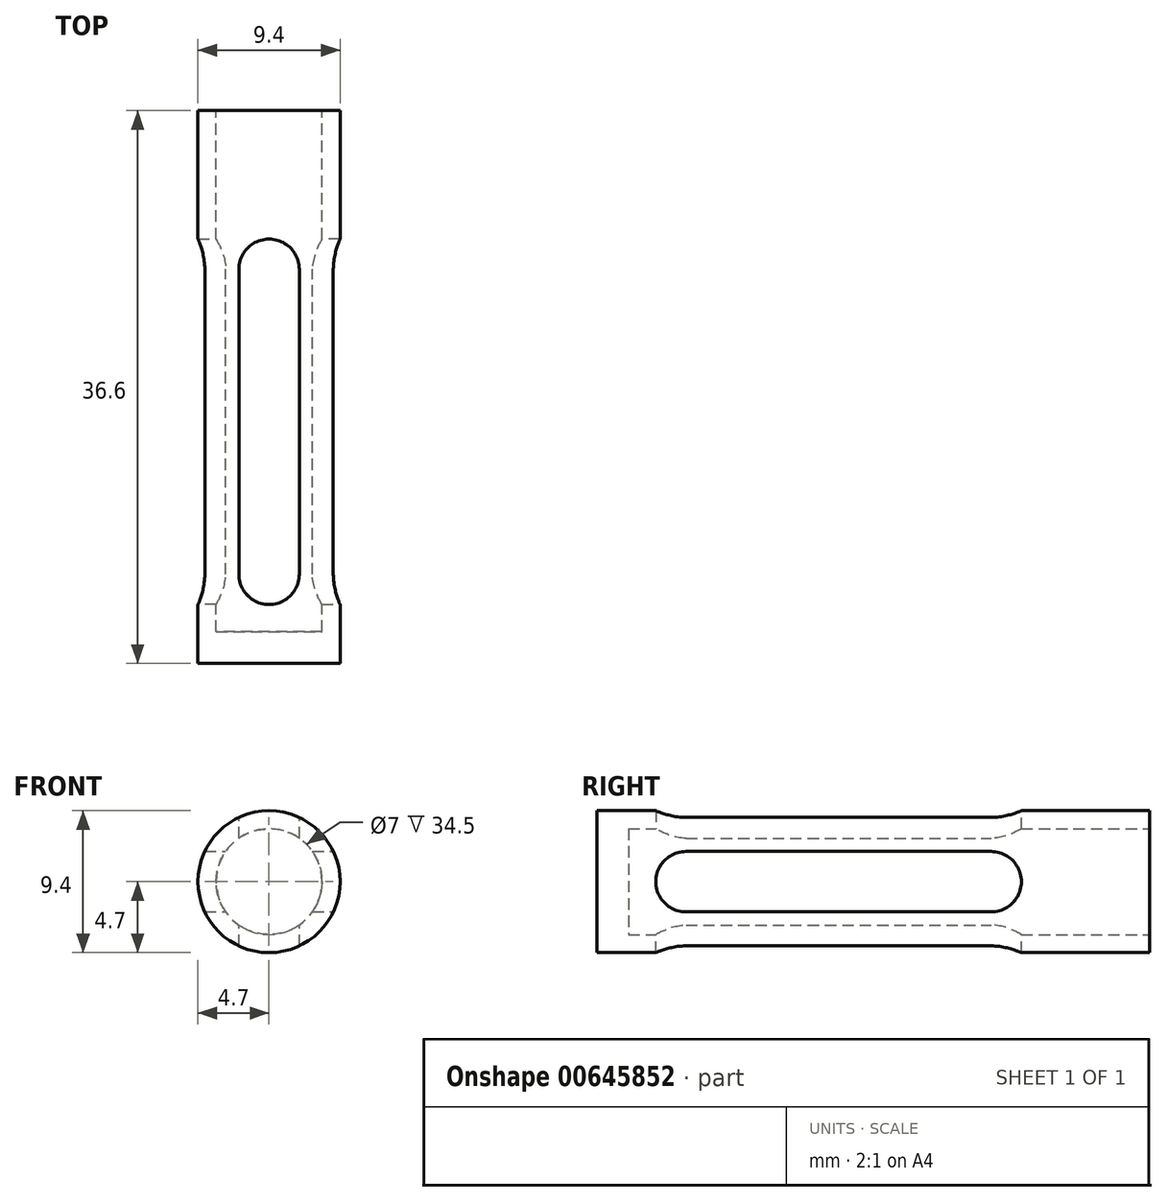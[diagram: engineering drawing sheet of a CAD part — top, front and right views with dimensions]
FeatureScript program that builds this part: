
annotation { "Feature Type Name" : "Feature", "Feature Type Description" : "" }
export const myFeature = defineFeature(function(context is Context, id is Id, definition is map)
    precondition{}
    {
        {
            var Q0;
            Q0=qCreatedBy(makeId("Front.planeOp"),FACE);
            var sketch = newSketch(context, id + "F0", { "sketchPlane" : qUnion([Q0])});
            skCircle(sketch, "E0", {"center": v(0, 0) * mm, "radius": 4.7 * mm});
            skSolve(sketch);
        }
        {
            var Q0;
            Q0 = qSketchRegion(id + "F0", true);
            extrude(context, id + "F1", {"entities" : qUnion([Q0]), "depth" : 36.6 * mm, "offsetDistance" : 25 * mm});
        }
        {
            var Q0;
            Q0=makeQuery(id+"F1.opExtrude","CAP_FACE",FACE,{"disambiguationData":[OSD([sQuery(id+"F0.wireOp",EDGE,"E0")])],"isStart":true});
            var sketch = newSketch(context, id + "F2", { "sketchPlane" : qUnion([Q0])});
            skCircle(sketch, "E1", {"center": v(0, 0) * mm, "radius": 3.5 * mm});
            skCircle(sketch, "E2.0", {"center": v(0, 0) * mm, "radius": 4.7 * mm, "construction": true});
            skSolve(sketch);
        }
        {
            var Q0;
            Q0=makeQuery(id+"F2.imprint","IMPRINT",FACE,{"disambiguationData":[TD([[makeQuery(id+"F2.imprint","IMPRINT",EDGE,{"derivedFrom":sQuery(id+"F2.wireOp",EDGE,"E1")}),1.0]])]});
            extrude(context, id + "F3", {"entities" : qUnion([Q0]), "operationType" : NewBodyOperationType.REMOVE, "oppositeDirection" : true, "depth" : 34.5 * mm, "offsetDistance" : 25 * mm});
        }
        {
            var Q0;
            Q0=qCreatedBy(makeId("Top.planeOp"),FACE);
            var sketch = newSketch(context, id + "F4", { "sketchPlane" : qUnion([Q0])});
            skLineSegment(sketch, "E3.bottom", {"start": v(-2, -32.7) * mm, "end": v(2, -32.7) * mm});
            skLineSegment(sketch, "E3.top", {"start": v(-2, -8.5) * mm, "end": v(2, -8.5) * mm});
            skLineSegment(sketch, "E3.left", {"start": v(-2, -32.7) * mm, "end": v(-2, -8.5) * mm});
            skLineSegment(sketch, "E3.right", {"start": v(2, -32.7) * mm, "end": v(2, -8.5) * mm});
            skLineSegment(sketch, "E4.0", {"start": v(4.7, -36.6) * mm, "end": v(-4.7, -36.6) * mm, "construction": true});
            skLineSegment(sketch, "E5.0", {"start": v(4.7, 0) * mm, "end": v(-4.7, 0) * mm, "construction": true});
            skSolve(sketch);
        }
        {
            var Q0;
            Q0 = qSketchRegion(id + "F4", true);
            extrude(context, id + "F5", {"entities" : qUnion([Q0]), "operationType" : NewBodyOperationType.REMOVE, "endBound" : BoundingType.SYMMETRIC, "oppositeDirection" : true, "depth" : 25 * mm, "offsetDistance" : 25 * mm});
        }
        {
            var Q0;
            Q0=qCreatedBy(makeId("Right.planeOp"),FACE);
            var sketch = newSketch(context, id + "F6", { "sketchPlane" : qUnion([Q0])});
            skLineSegment(sketch, "E6.bottom", {"start": v(-8.5, 2) * mm, "end": v(-32.7, 2) * mm});
            skLineSegment(sketch, "E6.top", {"start": v(-8.5, -2) * mm, "end": v(-32.7, -2) * mm});
            skLineSegment(sketch, "E6.left", {"start": v(-8.5, 2) * mm, "end": v(-8.5, -2) * mm});
            skLineSegment(sketch, "E6.right", {"start": v(-32.7, 2) * mm, "end": v(-32.7, -2) * mm});
            skLineSegment(sketch, "E7.0", {"start": v(-36.6, -4.7) * mm, "end": v(-36.6, 4.7) * mm, "construction": true});
            skLineSegment(sketch, "E8.0", {"start": v(0, -4.7) * mm, "end": v(0, 4.7) * mm, "construction": true});
            skSolve(sketch);
        }
        {
            var Q0;
            Q0 = qSketchRegion(id + "F6", true);
            extrude(context, id + "F7", {"entities" : qUnion([Q0]), "operationType" : NewBodyOperationType.REMOVE, "endBound" : BoundingType.SYMMETRIC, "oppositeDirection" : true, "depth" : 25 * mm, "offsetDistance" : 25 * mm});
        }
        {
            var Q0;
            Q0=makeQuery(id+"F5.boolean.opBoolean","COPY",EDGE,{"disambiguationData":[OD(0.0)],"derivedFrom":makeQuery(id+"F5.opExtrude","SWEPT_EDGE",EDGE,{"disambiguationData":[OSD([sQuery(id+"F4.wireOp",EDGE,"E3.top"),sQuery(id+"F4.wireOp",EDGE,"E3.right")])]})});
            var Q1;
            Q1=makeQuery(id+"F5.boolean.opBoolean","COPY",EDGE,{"disambiguationData":[OD(0.0)],"derivedFrom":makeQuery(id+"F5.opExtrude","SWEPT_EDGE",EDGE,{"disambiguationData":[OSD([sQuery(id+"F4.wireOp",EDGE,"E3.top"),sQuery(id+"F4.wireOp",EDGE,"E3.left")])]})});
            var Q2;
            Q2=makeQuery(id+"F7.boolean.opBoolean","COPY",EDGE,{"disambiguationData":[OD(1.0)],"derivedFrom":makeQuery(id+"F7.opExtrude","SWEPT_EDGE",EDGE,{"disambiguationData":[OSD([sQuery(id+"F6.wireOp",EDGE,"E6.top"),sQuery(id+"F6.wireOp",EDGE,"E6.left")])]})});
            var Q3;
            Q3=makeQuery(id+"F7.boolean.opBoolean","COPY",EDGE,{"disambiguationData":[OD(1.0)],"derivedFrom":makeQuery(id+"F7.opExtrude","SWEPT_EDGE",EDGE,{"disambiguationData":[OSD([sQuery(id+"F6.wireOp",EDGE,"E6.bottom"),sQuery(id+"F6.wireOp",EDGE,"E6.left")])]})});
            var Q4;
            Q4=makeQuery(id+"F7.boolean.opBoolean","COPY",EDGE,{"disambiguationData":[OD(0.0)],"derivedFrom":makeQuery(id+"F7.opExtrude","SWEPT_EDGE",EDGE,{"disambiguationData":[OSD([sQuery(id+"F6.wireOp",EDGE,"E6.bottom"),sQuery(id+"F6.wireOp",EDGE,"E6.left")])]})});
            var Q5;
            Q5=makeQuery(id+"F7.boolean.opBoolean","COPY",EDGE,{"disambiguationData":[OD(0.0)],"derivedFrom":makeQuery(id+"F7.opExtrude","SWEPT_EDGE",EDGE,{"disambiguationData":[OSD([sQuery(id+"F6.wireOp",EDGE,"E6.top"),sQuery(id+"F6.wireOp",EDGE,"E6.left")])]})});
            var Q6;
            Q6=makeQuery(id+"F5.boolean.opBoolean","COPY",EDGE,{"disambiguationData":[OD(1.0)],"derivedFrom":makeQuery(id+"F5.opExtrude","SWEPT_EDGE",EDGE,{"disambiguationData":[OSD([sQuery(id+"F4.wireOp",EDGE,"E3.top"),sQuery(id+"F4.wireOp",EDGE,"E3.right")])]})});
            var Q7;
            Q7=makeQuery(id+"F5.boolean.opBoolean","COPY",EDGE,{"disambiguationData":[OD(1.0)],"derivedFrom":makeQuery(id+"F5.opExtrude","SWEPT_EDGE",EDGE,{"disambiguationData":[OSD([sQuery(id+"F4.wireOp",EDGE,"E3.top"),sQuery(id+"F4.wireOp",EDGE,"E3.left")])]})});
            var Q8;
            Q8=makeQuery(id+"F7.boolean.opBoolean","COPY",EDGE,{"disambiguationData":[OD(0.0)],"derivedFrom":makeQuery(id+"F7.opExtrude","SWEPT_EDGE",EDGE,{"disambiguationData":[OSD([sQuery(id+"F6.wireOp",EDGE,"E6.bottom"),sQuery(id+"F6.wireOp",EDGE,"E6.right")])]})});
            var Q9;
            Q9=makeQuery(id+"F7.boolean.opBoolean","COPY",EDGE,{"disambiguationData":[OD(0.0)],"derivedFrom":makeQuery(id+"F7.opExtrude","SWEPT_EDGE",EDGE,{"disambiguationData":[OSD([sQuery(id+"F6.wireOp",EDGE,"E6.top"),sQuery(id+"F6.wireOp",EDGE,"E6.right")])]})});
            var Q10;
            Q10=makeQuery(id+"F5.boolean.opBoolean","COPY",EDGE,{"disambiguationData":[OD(0.0)],"derivedFrom":makeQuery(id+"F5.opExtrude","SWEPT_EDGE",EDGE,{"disambiguationData":[OSD([sQuery(id+"F4.wireOp",EDGE,"E3.bottom"),sQuery(id+"F4.wireOp",EDGE,"E3.left")])]})});
            var Q11;
            Q11=makeQuery(id+"F5.boolean.opBoolean","COPY",EDGE,{"disambiguationData":[OD(0.0)],"derivedFrom":makeQuery(id+"F5.opExtrude","SWEPT_EDGE",EDGE,{"disambiguationData":[OSD([sQuery(id+"F4.wireOp",EDGE,"E3.bottom"),sQuery(id+"F4.wireOp",EDGE,"E3.right")])]})});
            var Q12;
            Q12=makeQuery(id+"F7.boolean.opBoolean","COPY",EDGE,{"disambiguationData":[OD(1.0)],"derivedFrom":makeQuery(id+"F7.opExtrude","SWEPT_EDGE",EDGE,{"disambiguationData":[OSD([sQuery(id+"F6.wireOp",EDGE,"E6.top"),sQuery(id+"F6.wireOp",EDGE,"E6.right")])]})});
            var Q13;
            Q13=makeQuery(id+"F5.boolean.opBoolean","COPY",EDGE,{"disambiguationData":[OD(1.0)],"derivedFrom":makeQuery(id+"F5.opExtrude","SWEPT_EDGE",EDGE,{"disambiguationData":[OSD([sQuery(id+"F4.wireOp",EDGE,"E3.bottom"),sQuery(id+"F4.wireOp",EDGE,"E3.right")])]})});
            var Q14;
            Q14=makeQuery(id+"F5.boolean.opBoolean","COPY",EDGE,{"disambiguationData":[OD(1.0)],"derivedFrom":makeQuery(id+"F5.opExtrude","SWEPT_EDGE",EDGE,{"disambiguationData":[OSD([sQuery(id+"F4.wireOp",EDGE,"E3.bottom"),sQuery(id+"F4.wireOp",EDGE,"E3.left")])]})});
            var Q15;
            Q15=makeQuery(id+"F7.boolean.opBoolean","COPY",EDGE,{"disambiguationData":[OD(1.0)],"derivedFrom":makeQuery(id+"F7.opExtrude","SWEPT_EDGE",EDGE,{"disambiguationData":[OSD([sQuery(id+"F6.wireOp",EDGE,"E6.bottom"),sQuery(id+"F6.wireOp",EDGE,"E6.right")])]})});
            fillet(context, id + "F8", {"entities" : qUnion([Q0, Q1, Q2, Q3, Q4, Q5, Q6, Q7, Q8, Q9, Q10, Q11, Q12, Q13, Q14, Q15]), "radius" : 2 * mm, "tangentPropagation" : true, "allowEdgeOverflow" : false});
        }
    });
